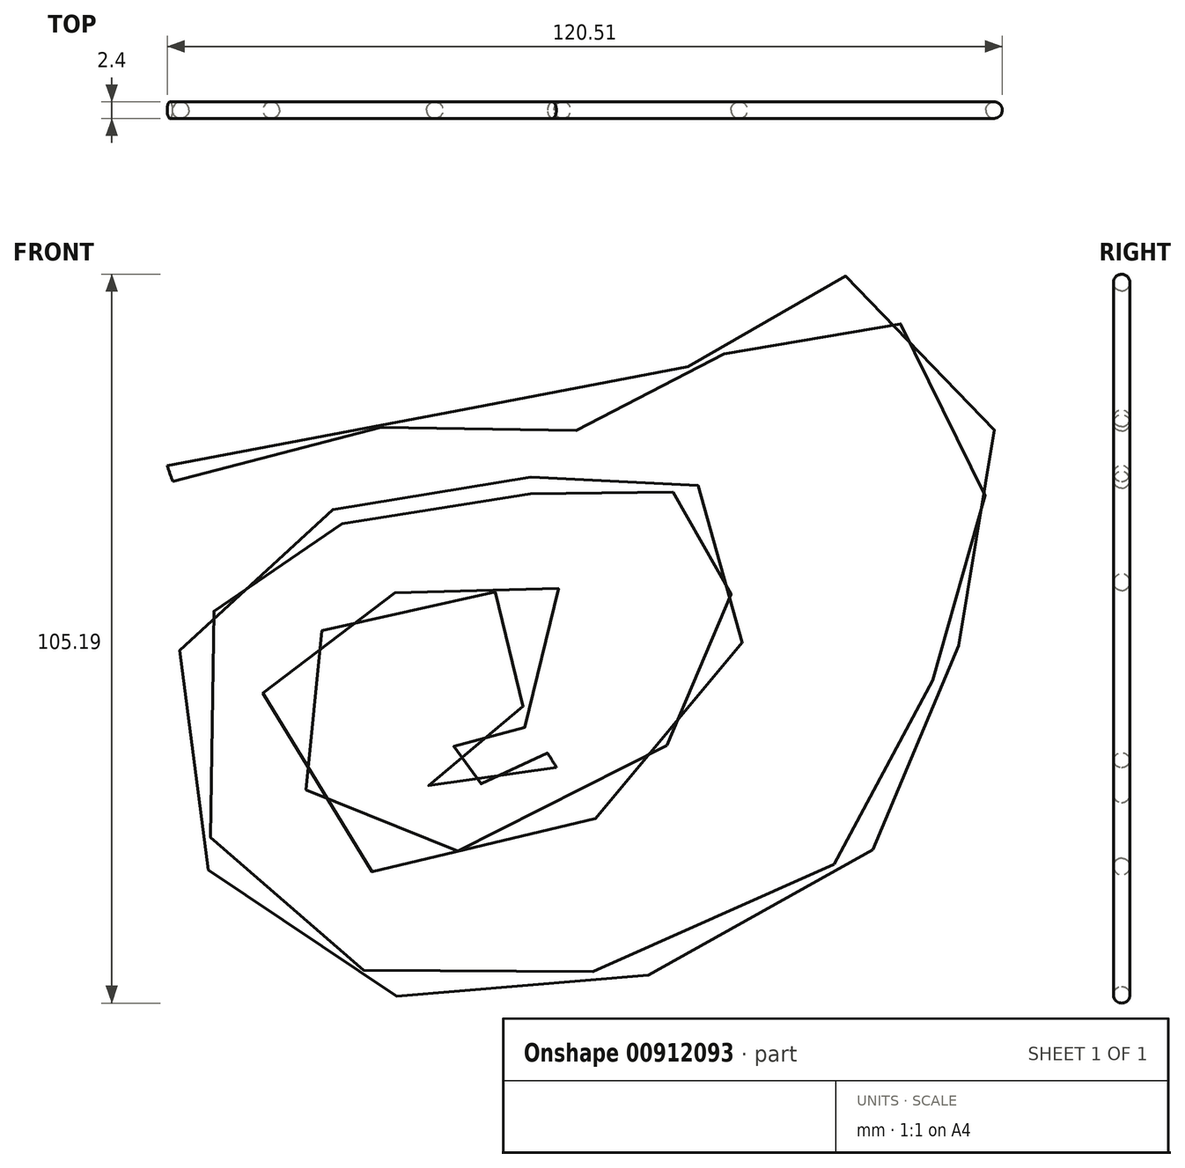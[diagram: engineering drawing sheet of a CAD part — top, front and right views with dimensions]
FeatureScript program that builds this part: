
annotation { "Feature Type Name" : "Feature", "Feature Type Description" : "" }
export const myFeature = defineFeature(function(context is Context, id is Id, definition is map)
    precondition{}
    {
        {
            var Q0;
            Q0=qCreatedBy(makeId("Front.planeOp"),FACE);
            var sketch = newSketch(context, id + "F0", { "sketchPlane" : qUnion([Q0])});
            skFitSpline(sketch, "E0", {"points": [v(-55.21, 41.33) * mm, v(-29.73, 48.67) * mm, v(-10.22, 48.9) * mm, v(9.99, 49.6) * mm, v(20.55, 56.02) * mm, v(39.37, 68.88) * mm, v(59.58, 53.03) * mm, v(62.8, 36.73) * mm, v(57.05, 17.9) * mm, v(49.7, -4.82) * mm, v(27.2, -23.88) * mm, v(-11.82, -33.06) * mm, v(-33.63, -28) * mm, v(-50.62, -10.1) * mm, v(-50.62, 20.66) * mm, v(-41.21, 28.93) * mm, v(-27.66, 36.5) * mm, v(-6.08, 39.49) * mm, v(4.7, 39.95) * mm, v(16.87, 39.95) * mm, v(23.3, 35.36) * mm, v(26.29, 25.71) * mm, v(24.22, 13.32) * mm, v(10.9, -3.21) * mm, v(-18.02, -14.23) * mm, v(-32.26, -10.33) * mm, v(-40.06, 12.4) * mm, v(-31.57, 20.66) * mm, v(-15.96, 24.1) * mm, v(0, 23.42) * mm, v(-5.17, 6.43) * mm, v(-14.8, 4.13) * mm, v(-17.1, -3.44) * mm, v(-9.07, -4.36) * mm, v(0, 0) * mm], "startDerivative": vector(734.73, 257.48) * mm, "endDerivative": vector(376.74, 231.1) * mm});
            skSolve(sketch);
        }
        {
            var Q0;
            Q0=sQuery(id+"F0.wireOp",VERTEX,"E0.start");
            var Q1;
            Q1=sQuery(id+"F0.wireOp",EDGE,"E0");
            cPlane(context, id + "F1", {"entities" : qUnion([Q0, Q1]), "cplaneType" : CPlaneType.CURVE_POINT, "offset" : 25.4 * mm, "width" : 152.4 * mm, "height" : 152.4 * mm});
        }
        {
            var Q0;
            Q0=qCreatedBy(id+"F1.planeOp",FACE);
            var sketch = newSketch(context, id + "F2", { "sketchPlane" : qUnion([Q0])});
            skCircle(sketch, "E1", {"center": v(0, 57.69) * mm, "radius": 1.2 * mm});
            skSolve(sketch);
        }
        {
            var Q0;
            Q0=makeQuery(id+"F2.imprint","IMPRINT",FACE,{"disambiguationData":[TD([[makeQuery(id+"F2.imprint","IMPRINT",EDGE,{"derivedFrom":sQuery(id+"F2.wireOp",EDGE,"E1")}),1.0]])]});
            var Q1;
            Q1=sQuery(id+"F0.wireOp",EDGE,"E0");
            sweep(context, id + "F3", {"profiles" : qUnion([Q0]), "path" : qUnion([Q1])});
        }
    });
